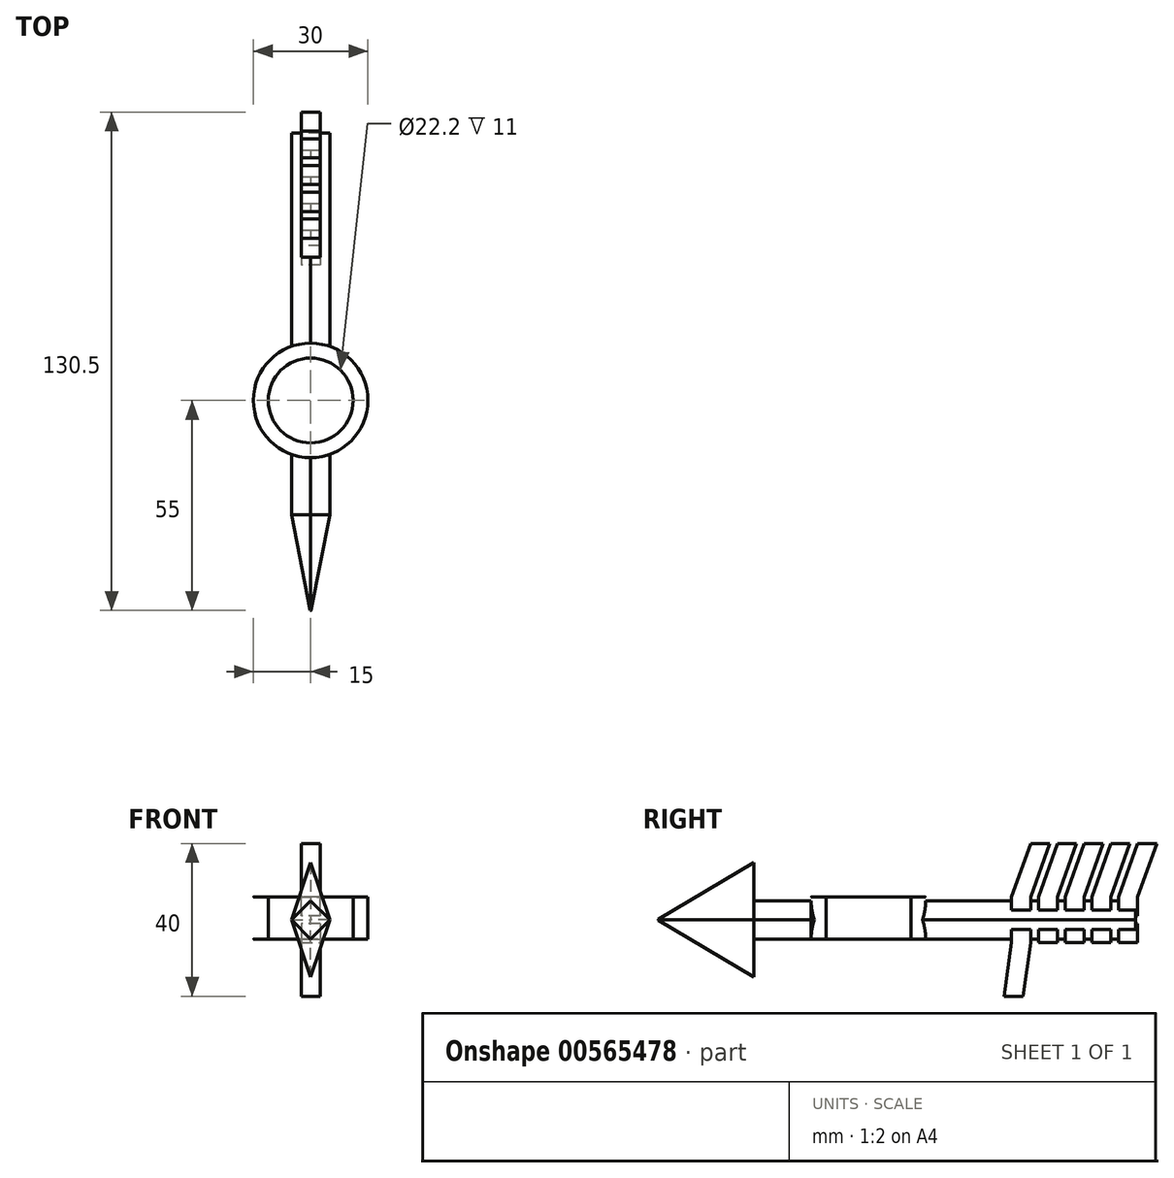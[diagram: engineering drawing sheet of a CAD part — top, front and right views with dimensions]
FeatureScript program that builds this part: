
annotation { "Feature Type Name" : "Feature", "Feature Type Description" : "" }
export const myFeature = defineFeature(function(context is Context, id is Id, definition is map)
    precondition{}
    {
        {
            var Q0;
            Q0=qCreatedBy(makeId("Front.planeOp"),FACE);
            var sketch = newSketch(context, id + "F0", { "sketchPlane" : qUnion([Q0])});
            skPoint(sketch, "E0", {"position": v(0, 15) * mm});
            skPoint(sketch, "E1", {"position": v(0, -15) * mm});
            skPoint(sketch, "E2", {"position": v(5, 0) * mm});
            skPoint(sketch, "E3", {"position": v(-5, 0) * mm});
            skLineSegment(sketch, "E4", {"start": v(0, 15) * mm, "end": v(-5, 0) * mm});
            skLineSegment(sketch, "E5", {"start": v(-5, 0) * mm, "end": v(0, -15) * mm});
            skLineSegment(sketch, "E6", {"start": v(0, -15) * mm, "end": v(5, 0) * mm});
            skLineSegment(sketch, "E7", {"start": v(5, 0) * mm, "end": v(0, 15) * mm});
            skSolve(sketch);
        }
        {
            var Q0;
            Q0=qCreatedBy(makeId("Front.planeOp"),FACE);
            cPlane(context, id + "F1", {"entities" : qUnion([Q0]), "cplaneType" : CPlaneType.OFFSET, "offset" : 25 * mm, "width" : 150 * mm, "height" : 150 * mm});
        }
        {
            var Q0;
            Q0=qCreatedBy(id+"F1.planeOp",FACE);
            var sketch = newSketch(context, id + "F2", { "sketchPlane" : qUnion([Q0])});
            skPoint(sketch, "E8", {"position": v(0, 0) * mm});
            skCircle(sketch, "E9", {"center": v(0, 0) * mm, "radius": 0.1 * mm});
            skPoint(sketch, "E10", {"position": v(0, 0.1) * mm});
            skPoint(sketch, "E11", {"position": v(0, -0.1) * mm});
            skPoint(sketch, "E12", {"position": v(-0.1, 0) * mm});
            skPoint(sketch, "E13", {"position": v(0.1, 0) * mm});
            skSolve(sketch);
        }
        {
            var Q0;
            Q0=makeQuery(id+"F0.imprint","IMPRINT",FACE,{"disambiguationData":[TD([[makeQuery(id+"F0.imprint","IMPRINT",EDGE,{"derivedFrom":sQuery(id+"F0.wireOp",EDGE,"E4")}),1.0]])]});
            var Q1;
            Q1=makeQuery(id+"F2.imprint","IMPRINT",FACE,{"disambiguationData":[TD([[makeQuery(id+"F2.imprint","IMPRINT",EDGE,{"derivedFrom":sQuery(id+"F2.wireOp",EDGE,"E9")}),1.0]])]});
            loft(context, id + "F3", {"sheetProfilesArray" : [{ "sheetProfileEntities" : qUnion([Q0]) }, { "sheetProfileEntities" : qUnion([Q1]) }]});
        }
        {
            var Q0;
            Q0=qCreatedBy(makeId("Front.planeOp"),FACE);
            var sketch = newSketch(context, id + "F4", { "sketchPlane" : qUnion([Q0])});
            skCircle(sketch, "E14.cCircle", {"center": v(0, 0) * mm, "radius": 5 * mm, "construction": true});
            skLineSegment(sketch, "E14.0", {"start": v(-5, 0) * mm, "end": v(0, 5) * mm});
            skLineSegment(sketch, "E14.1", {"start": v(0, 5) * mm, "end": v(5, 0) * mm});
            skLineSegment(sketch, "E14.2", {"start": v(5, 0) * mm, "end": v(0, -5) * mm});
            skLineSegment(sketch, "E14.3", {"start": v(0, -5) * mm, "end": v(-5, 0) * mm});
            skSolve(sketch);
        }
        {
            var Q0;
            Q0 = qSketchRegion(id + "F4", true);
            var Q1;
            Q1=makeQuery(id+"F4.imprint","IMPRINT",FACE,{"disambiguationData":[TD([[makeQuery(id+"F4.imprint","IMPRINT",EDGE,{"derivedFrom":sQuery(id+"F4.wireOp",EDGE,"E14.0")}),-1.0]])]});
            extrude(context, id + "F5", {"entities" : qUnion([Q0, Q1]), "operationType" : NewBodyOperationType.ADD, "oppositeDirection" : true, "depth" : 100 * mm, "offsetDistance" : 25 * mm});
        }
        {
            var Q0;
            Q0=qCreatedBy(makeId("Top.planeOp"),FACE);
            cPlane(context, id + "F6", {"entities" : qUnion([Q0]), "cplaneType" : CPlaneType.OFFSET, "offset" : 6 * mm, "width" : 150 * mm, "height" : 150 * mm});
        }
        {
            var Q0;
            Q0=qCreatedBy(id+"F6.planeOp",FACE);
            var sketch = newSketch(context, id + "F7", { "sketchPlane" : qUnion([Q0])});
            skPoint(sketch, "E15", {"position": v(0, 30) * mm});
            skCircle(sketch, "E16", {"center": v(0, 30) * mm, "radius": 15 * mm});
            skCircle(sketch, "E17", {"center": v(0, 30) * mm, "radius": 11 * mm});
            skSolve(sketch);
        }
        {
            var Q0;
            Q0 = qSketchRegion(id + "F7", true);
            extrude(context, id + "F8", {"entities" : qUnion([Q0]), "operationType" : NewBodyOperationType.ADD, "oppositeDirection" : true, "depth" : 11 * mm, "offsetDistance" : 25 * mm});
        }
        {
            var Q0;
            Q0=qCreatedBy(id+"F6.planeOp",FACE);
            var sketch = newSketch(context, id + "F9", { "sketchPlane" : qUnion([Q0])});
            skPoint(sketch, "E18", {"position": v(0, 30) * mm});
            skCircle(sketch, "E19", {"center": v(0, 30) * mm, "radius": 11.1 * mm});
            skSolve(sketch);
        }
        {
            var Q0;
            Q0=makeQuery(id+"F9.imprint","IMPRINT",FACE,{"disambiguationData":[TD([[makeQuery(id+"F9.imprint","IMPRINT",EDGE,{"derivedFrom":sQuery(id+"F9.wireOp",EDGE,"E19")}),1.0]])]});
            extrude(context, id + "F10", {"entities" : qUnion([Q0]), "operationType" : NewBodyOperationType.REMOVE, "endBound" : BoundingType.THROUGH_ALL, "oppositeDirection" : true, "depth" : 25 * mm, "offsetDistance" : 25 * mm});
        }
        {
            var Q0;
            Q0=qCreatedBy(id+"F6.planeOp",FACE);
            var sketch = newSketch(context, id + "F11", { "sketchPlane" : qUnion([Q0])});
            skPoint(sketch, "E20", {"position": v(0, 70) * mm});
            skLineSegment(sketch, "E21.bottom", {"start": v(2.5, 72.5) * mm, "end": v(-2.5, 72.5) * mm});
            skLineSegment(sketch, "E21.top", {"start": v(2.5, 67.5) * mm, "end": v(-2.5, 67.5) * mm});
            skLineSegment(sketch, "E21.left", {"start": v(2.5, 72.5) * mm, "end": v(2.5, 67.5) * mm});
            skLineSegment(sketch, "E21.right", {"start": v(-2.5, 72.5) * mm, "end": v(-2.5, 67.5) * mm});
            skPoint(sketch, "E22", {"position": v(-2.5, 67.5) * mm});
            skPoint(sketch, "E23", {"position": v(-2.5, 72.5) * mm});
            skPoint(sketch, "E24", {"position": v(2.5, 72.5) * mm});
            skPoint(sketch, "E25", {"position": v(2.5, 67.5) * mm});
            skPoint(sketch, "E26", {"position": v(0, 77) * mm});
            skPoint(sketch, "E27", {"position": v(0, 84) * mm});
            skPoint(sketch, "E28", {"position": v(0, 91) * mm});
            skPoint(sketch, "E29", {"position": v(0, 98) * mm});
            skLineSegment(sketch, "E30.bottom", {"start": v(2.5, 79.5) * mm, "end": v(-2.5, 79.5) * mm});
            skLineSegment(sketch, "E30.top", {"start": v(2.5, 74.5) * mm, "end": v(-2.5, 74.5) * mm});
            skLineSegment(sketch, "E30.left", {"start": v(2.5, 79.5) * mm, "end": v(2.5, 74.5) * mm});
            skLineSegment(sketch, "E30.right", {"start": v(-2.5, 79.5) * mm, "end": v(-2.5, 74.5) * mm});
            skLineSegment(sketch, "E31.bottom", {"start": v(2.5, 86.5) * mm, "end": v(-2.5, 86.5) * mm});
            skLineSegment(sketch, "E31.top", {"start": v(2.5, 81.5) * mm, "end": v(-2.5, 81.5) * mm});
            skLineSegment(sketch, "E31.left", {"start": v(2.5, 86.5) * mm, "end": v(2.5, 81.5) * mm});
            skLineSegment(sketch, "E31.right", {"start": v(-2.5, 86.5) * mm, "end": v(-2.5, 81.5) * mm});
            skLineSegment(sketch, "E32.bottom", {"start": v(2.5, 93.5) * mm, "end": v(-2.5, 93.5) * mm});
            skLineSegment(sketch, "E32.top", {"start": v(2.5, 88.5) * mm, "end": v(-2.5, 88.5) * mm});
            skLineSegment(sketch, "E32.left", {"start": v(2.5, 93.5) * mm, "end": v(2.5, 88.5) * mm});
            skLineSegment(sketch, "E32.right", {"start": v(-2.5, 93.5) * mm, "end": v(-2.5, 88.5) * mm});
            skLineSegment(sketch, "E33.bottom", {"start": v(2.5, 100.5) * mm, "end": v(-2.5, 100.5) * mm});
            skLineSegment(sketch, "E33.top", {"start": v(2.5, 95.5) * mm, "end": v(-2.5, 95.5) * mm});
            skLineSegment(sketch, "E33.left", {"start": v(2.5, 100.5) * mm, "end": v(2.5, 95.5) * mm});
            skLineSegment(sketch, "E33.right", {"start": v(-2.5, 100.5) * mm, "end": v(-2.5, 95.5) * mm});
            skPoint(sketch, "E34", {"position": v(-2.5, 74.5) * mm});
            skPoint(sketch, "E35", {"position": v(-2.5, 79.5) * mm});
            skPoint(sketch, "E36", {"position": v(2.5, 79.5) * mm});
            skPoint(sketch, "E37", {"position": v(2.5, 74.5) * mm});
            skPoint(sketch, "E38", {"position": v(-2.5, 81.5) * mm});
            skPoint(sketch, "E39", {"position": v(-2.5, 86.5) * mm});
            skPoint(sketch, "E40", {"position": v(2.5, 86.5) * mm});
            skPoint(sketch, "E41", {"position": v(2.5, 81.5) * mm});
            skPoint(sketch, "E42", {"position": v(-2.5, 88.5) * mm});
            skPoint(sketch, "E43", {"position": v(-2.5, 93.5) * mm});
            skPoint(sketch, "E44", {"position": v(2.5, 93.5) * mm});
            skPoint(sketch, "E45", {"position": v(2.5, 88.5) * mm});
            skPoint(sketch, "E46", {"position": v(-2.5, 95.5) * mm});
            skPoint(sketch, "E47", {"position": v(-2.5, 100.5) * mm});
            skPoint(sketch, "E48", {"position": v(2.5, 100.5) * mm});
            skPoint(sketch, "E49", {"position": v(2.5, 95.5) * mm});
            skSolve(sketch);
        }
        {
            var Q0;
            Q0=qCreatedBy(makeId("Top.planeOp"),FACE);
            cPlane(context, id + "F12", {"entities" : qUnion([Q0]), "cplaneType" : CPlaneType.OFFSET, "offset" : 20 * mm, "width" : 150 * mm, "height" : 150 * mm});
        }
        {
            var Q0;
            Q0=qCreatedBy(id+"F12.planeOp",FACE);
            var sketch = newSketch(context, id + "F13", { "sketchPlane" : qUnion([Q0])});
            skPoint(sketch, "E50", {"position": v(0, 75) * mm});
            skPoint(sketch, "E51", {"position": v(0, 82) * mm});
            skPoint(sketch, "E52", {"position": v(0, 89) * mm});
            skPoint(sketch, "E53", {"position": v(0, 96) * mm});
            skLineSegment(sketch, "E54", {"start": v(0, 0) * mm, "end": v(0, 100) * mm, "construction": true});
            skPoint(sketch, "E55", {"position": v(0, 103) * mm});
            skLineSegment(sketch, "E56.bottom", {"start": v(2.5, 77.5) * mm, "end": v(-2.5, 77.5) * mm});
            skLineSegment(sketch, "E56.top", {"start": v(2.5, 72.5) * mm, "end": v(-2.5, 72.5) * mm});
            skLineSegment(sketch, "E56.left", {"start": v(2.5, 77.5) * mm, "end": v(2.5, 72.5) * mm});
            skLineSegment(sketch, "E56.right", {"start": v(-2.5, 77.5) * mm, "end": v(-2.5, 72.5) * mm});
            skLineSegment(sketch, "E57.bottom", {"start": v(2.5, 84.5) * mm, "end": v(-2.5, 84.5) * mm});
            skLineSegment(sketch, "E57.top", {"start": v(2.5, 79.5) * mm, "end": v(-2.5, 79.5) * mm});
            skLineSegment(sketch, "E57.left", {"start": v(2.5, 84.5) * mm, "end": v(2.5, 79.5) * mm});
            skLineSegment(sketch, "E57.right", {"start": v(-2.5, 84.5) * mm, "end": v(-2.5, 79.5) * mm});
            skLineSegment(sketch, "E58.bottom", {"start": v(2.5, 91.5) * mm, "end": v(-2.5, 91.5) * mm});
            skLineSegment(sketch, "E58.top", {"start": v(2.5, 86.5) * mm, "end": v(-2.5, 86.5) * mm});
            skLineSegment(sketch, "E58.left", {"start": v(2.5, 91.5) * mm, "end": v(2.5, 86.5) * mm});
            skLineSegment(sketch, "E58.right", {"start": v(-2.5, 91.5) * mm, "end": v(-2.5, 86.5) * mm});
            skLineSegment(sketch, "E59.bottom", {"start": v(2.5, 98.5) * mm, "end": v(-2.5, 98.5) * mm});
            skLineSegment(sketch, "E59.top", {"start": v(2.5, 93.5) * mm, "end": v(-2.5, 93.5) * mm});
            skLineSegment(sketch, "E59.left", {"start": v(2.5, 98.5) * mm, "end": v(2.5, 93.5) * mm});
            skLineSegment(sketch, "E59.right", {"start": v(-2.5, 98.5) * mm, "end": v(-2.5, 93.5) * mm});
            skLineSegment(sketch, "E60.bottom", {"start": v(2.5, 105.5) * mm, "end": v(-2.5, 105.5) * mm});
            skLineSegment(sketch, "E60.top", {"start": v(2.5, 100.5) * mm, "end": v(-2.5, 100.5) * mm});
            skLineSegment(sketch, "E60.left", {"start": v(2.5, 105.5) * mm, "end": v(2.5, 100.5) * mm});
            skLineSegment(sketch, "E60.right", {"start": v(-2.5, 105.5) * mm, "end": v(-2.5, 100.5) * mm});
            skSolve(sketch);
        }
        {
            var Q0;
            Q0=makeQuery(id+"F11.imprint","IMPRINT",FACE,{"disambiguationData":[TD([[makeQuery(id+"F11.imprint","IMPRINT",EDGE,{"derivedFrom":sQuery(id+"F11.wireOp",EDGE,"E21.bottom")}),1.0]])]});
            var Q1;
            Q1=makeQuery(id+"F11.imprint","IMPRINT",FACE,{"disambiguationData":[TD([[makeQuery(id+"F11.imprint","IMPRINT",EDGE,{"derivedFrom":sQuery(id+"F11.wireOp",EDGE,"E30.bottom")}),1.0]])]});
            var Q2;
            Q2=makeQuery(id+"F11.imprint","IMPRINT",FACE,{"disambiguationData":[TD([[makeQuery(id+"F11.imprint","IMPRINT",EDGE,{"derivedFrom":sQuery(id+"F11.wireOp",EDGE,"E31.bottom")}),1.0]])]});
            var Q3;
            Q3=makeQuery(id+"F11.imprint","IMPRINT",FACE,{"disambiguationData":[TD([[makeQuery(id+"F11.imprint","IMPRINT",EDGE,{"derivedFrom":sQuery(id+"F11.wireOp",EDGE,"E32.bottom")}),1.0]])]});
            var Q4;
            Q4=makeQuery(id+"F11.imprint","IMPRINT",FACE,{"disambiguationData":[TD([[makeQuery(id+"F11.imprint","IMPRINT",EDGE,{"derivedFrom":sQuery(id+"F11.wireOp",EDGE,"E33.bottom")}),1.0]])]});
            extrude(context, id + "F14", {"entities" : qUnion([Q0, Q1, Q2, Q3, Q4]), "operationType" : NewBodyOperationType.ADD, "oppositeDirection" : true, "depth" : 5 * mm, "offsetDistance" : 25 * mm});
        }
        {
            var Q1;
            Q1=makeQuery(id+"F14.opExtrude","CAP_FACE",FACE,{"disambiguationData":[OSD([sQuery(id+"F11.wireOp",EDGE,"E21.bottom"),sQuery(id+"F11.wireOp",EDGE,"E21.top"),sQuery(id+"F11.wireOp",EDGE,"E21.left"),sQuery(id+"F11.wireOp",EDGE,"E21.right")])],"isStart":true});
            var Q2;
            Q2=makeQuery(id+"F13.imprint","IMPRINT",FACE,{"disambiguationData":[TD([[makeQuery(id+"F13.imprint","IMPRINT",EDGE,{"derivedFrom":sQuery(id+"F13.wireOp",EDGE,"E56.bottom")}),1.0]])]});
            loft(context, id + "F15", {"operationType" : NewBodyOperationType.ADD, "sheetProfilesArray" : [{ "sheetProfileEntities" : qUnion([Q1]) }, { "sheetProfileEntities" : qUnion([Q2]) }]});
        }
        {
            var Q1;
            Q1=makeQuery(id+"F14.opExtrude","CAP_FACE",FACE,{"disambiguationData":[OSD([sQuery(id+"F11.wireOp",EDGE,"E30.bottom"),sQuery(id+"F11.wireOp",EDGE,"E30.top"),sQuery(id+"F11.wireOp",EDGE,"E30.left"),sQuery(id+"F11.wireOp",EDGE,"E30.right")])],"isStart":true});
            var Q2;
            Q2=makeQuery(id+"F13.imprint","IMPRINT",FACE,{"disambiguationData":[TD([[makeQuery(id+"F13.imprint","IMPRINT",EDGE,{"derivedFrom":sQuery(id+"F13.wireOp",EDGE,"E57.bottom")}),1.0]])]});
            loft(context, id + "F16", {"operationType" : NewBodyOperationType.ADD, "sheetProfilesArray" : [{ "sheetProfileEntities" : qUnion([Q1]) }, { "sheetProfileEntities" : qUnion([Q2]) }]});
        }
        {
            var Q1;
            Q1=makeQuery(id+"F14.opExtrude","CAP_FACE",FACE,{"disambiguationData":[OSD([sQuery(id+"F11.wireOp",EDGE,"E31.bottom"),sQuery(id+"F11.wireOp",EDGE,"E31.top"),sQuery(id+"F11.wireOp",EDGE,"E31.left"),sQuery(id+"F11.wireOp",EDGE,"E31.right")])],"isStart":true});
            var Q2;
            Q2=makeQuery(id+"F13.imprint","IMPRINT",FACE,{"disambiguationData":[TD([[makeQuery(id+"F13.imprint","IMPRINT",EDGE,{"derivedFrom":sQuery(id+"F13.wireOp",EDGE,"E58.bottom")}),1.0]])]});
            loft(context, id + "F17", {"operationType" : NewBodyOperationType.ADD, "sheetProfilesArray" : [{ "sheetProfileEntities" : qUnion([Q1]) }, { "sheetProfileEntities" : qUnion([Q2]) }]});
        }
        {
            var Q1;
            Q1=makeQuery(id+"F14.opExtrude","CAP_FACE",FACE,{"disambiguationData":[OSD([sQuery(id+"F11.wireOp",EDGE,"E32.bottom"),sQuery(id+"F11.wireOp",EDGE,"E32.top"),sQuery(id+"F11.wireOp",EDGE,"E32.left"),sQuery(id+"F11.wireOp",EDGE,"E32.right")])],"isStart":true});
            var Q2;
            Q2=makeQuery(id+"F13.imprint","IMPRINT",FACE,{"disambiguationData":[TD([[makeQuery(id+"F13.imprint","IMPRINT",EDGE,{"derivedFrom":sQuery(id+"F13.wireOp",EDGE,"E59.bottom")}),1.0]])]});
            loft(context, id + "F18", {"operationType" : NewBodyOperationType.ADD, "sheetProfilesArray" : [{ "sheetProfileEntities" : qUnion([Q1]) }, { "sheetProfileEntities" : qUnion([Q2]) }]});
        }
        {
            var Q1;
            Q1=makeQuery(id+"F14.opExtrude","CAP_FACE",FACE,{"disambiguationData":[OSD([sQuery(id+"F11.wireOp",EDGE,"E33.bottom"),sQuery(id+"F11.wireOp",EDGE,"E33.top"),sQuery(id+"F11.wireOp",EDGE,"E33.left"),sQuery(id+"F11.wireOp",EDGE,"E33.right")])],"isStart":true});
            var Q2;
            Q2=makeQuery(id+"F13.imprint","IMPRINT",FACE,{"disambiguationData":[TD([[makeQuery(id+"F13.imprint","IMPRINT",EDGE,{"derivedFrom":sQuery(id+"F13.wireOp",EDGE,"E60.bottom")}),1.0]])]});
            loft(context, id + "F19", {"operationType" : NewBodyOperationType.ADD, "sheetProfilesArray" : [{ "sheetProfileEntities" : qUnion([Q1]) }, { "sheetProfileEntities" : qUnion([Q2]) }]});
        }
        {
            var Q0;
            Q0=qCreatedBy(makeId("Top.planeOp"),FACE);
            cPlane(context, id + "F20", {"entities" : qUnion([Q0]), "cplaneType" : CPlaneType.OFFSET, "offset" : 6 * mm, "oppositeDirection" : true, "width" : 150 * mm, "height" : 150 * mm});
        }
        {
            var Q0;
            Q0=qCreatedBy(id+"F20.planeOp",FACE);
            var sketch = newSketch(context, id + "F21", { "sketchPlane" : qUnion([Q0])});
            skPoint(sketch, "E61", {"position": v(0, 70) * mm});
            skPoint(sketch, "E62", {"position": v(0, 77) * mm});
            skPoint(sketch, "E63", {"position": v(0, 84) * mm});
            skPoint(sketch, "E64", {"position": v(0, 91) * mm});
            skPoint(sketch, "E65", {"position": v(0, 98) * mm});
            skLineSegment(sketch, "E66.bottom", {"start": v(-2.5, 67.5) * mm, "end": v(2.5, 67.5) * mm});
            skLineSegment(sketch, "E66.top", {"start": v(-2.5, 72.5) * mm, "end": v(2.5, 72.5) * mm});
            skLineSegment(sketch, "E66.left", {"start": v(-2.5, 67.5) * mm, "end": v(-2.5, 72.5) * mm});
            skLineSegment(sketch, "E66.right", {"start": v(2.5, 67.5) * mm, "end": v(2.5, 72.5) * mm});
            skLineSegment(sketch, "E67.bottom", {"start": v(-2.5, 74.5) * mm, "end": v(2.5, 74.5) * mm});
            skLineSegment(sketch, "E67.top", {"start": v(-2.5, 79.5) * mm, "end": v(2.5, 79.5) * mm});
            skLineSegment(sketch, "E67.left", {"start": v(-2.5, 74.5) * mm, "end": v(-2.5, 79.5) * mm});
            skLineSegment(sketch, "E67.right", {"start": v(2.5, 74.5) * mm, "end": v(2.5, 79.5) * mm});
            skLineSegment(sketch, "E68.bottom", {"start": v(-2.5, 81.5) * mm, "end": v(2.5, 81.5) * mm});
            skLineSegment(sketch, "E68.top", {"start": v(-2.5, 86.5) * mm, "end": v(2.5, 86.5) * mm});
            skLineSegment(sketch, "E68.left", {"start": v(-2.5, 81.5) * mm, "end": v(-2.5, 86.5) * mm});
            skLineSegment(sketch, "E68.right", {"start": v(2.5, 81.5) * mm, "end": v(2.5, 86.5) * mm});
            skLineSegment(sketch, "E69.bottom", {"start": v(-2.5, 88.5) * mm, "end": v(2.5, 88.5) * mm});
            skLineSegment(sketch, "E69.top", {"start": v(-2.5, 93.5) * mm, "end": v(2.5, 93.5) * mm});
            skLineSegment(sketch, "E69.left", {"start": v(-2.5, 88.5) * mm, "end": v(-2.5, 93.5) * mm});
            skLineSegment(sketch, "E69.right", {"start": v(2.5, 88.5) * mm, "end": v(2.5, 93.5) * mm});
            skLineSegment(sketch, "E70.bottom", {"start": v(-2.5, 95.5) * mm, "end": v(2.5, 95.5) * mm});
            skLineSegment(sketch, "E70.top", {"start": v(-2.5, 100.5) * mm, "end": v(2.5, 100.5) * mm});
            skLineSegment(sketch, "E70.left", {"start": v(-2.5, 95.5) * mm, "end": v(-2.5, 100.5) * mm});
            skLineSegment(sketch, "E70.right", {"start": v(2.5, 95.5) * mm, "end": v(2.5, 100.5) * mm});
            skSolve(sketch);
        }
        {
            var Q0;
            Q0 = qSketchRegion(id + "F21", true);
            extrude(context, id + "F22", {"entities" : qUnion([Q0]), "operationType" : NewBodyOperationType.ADD, "depth" : 5 * mm, "offsetDistance" : 25 * mm});
        }
        {
            var Q0;
            Q0=qCreatedBy(makeId("Top.planeOp"),FACE);
            cPlane(context, id + "F23", {"entities" : qUnion([Q0]), "cplaneType" : CPlaneType.OFFSET, "offset" : 20 * mm, "oppositeDirection" : true, "width" : 150 * mm, "height" : 150 * mm});
        }
        {
            var Q0;
            Q0=qCreatedBy(id+"F23.planeOp",FACE);
            var sketch = newSketch(context, id + "F24", { "sketchPlane" : qUnion([Q0])});
            skPoint(sketch, "E71", {"position": v(0, 68) * mm});
            skPoint(sketch, "E72", {"position": v(0, 75) * mm});
            skPoint(sketch, "E73", {"position": v(0, 83.73) * mm});
            skPoint(sketch, "E74", {"position": v(0, 90.86) * mm});
            skPoint(sketch, "E75", {"position": v(0, 98.09) * mm});
            skLineSegment(sketch, "E76.bottom", {"start": v(2.5, 77.5) * mm, "end": v(-2.5, 77.5) * mm});
            skLineSegment(sketch, "E76.top", {"start": v(2.5, 72.5) * mm, "end": v(-2.5, 72.5) * mm});
            skLineSegment(sketch, "E76.left", {"start": v(2.5, 77.5) * mm, "end": v(2.5, 72.5) * mm});
            skLineSegment(sketch, "E76.right", {"start": v(-2.5, 77.5) * mm, "end": v(-2.5, 72.5) * mm});
            skLineSegment(sketch, "E77.bottom", {"start": v(2.5, 70.5) * mm, "end": v(-2.5, 70.5) * mm});
            skLineSegment(sketch, "E77.top", {"start": v(2.5, 65.5) * mm, "end": v(-2.5, 65.5) * mm});
            skLineSegment(sketch, "E77.left", {"start": v(2.5, 70.5) * mm, "end": v(2.5, 65.5) * mm});
            skLineSegment(sketch, "E77.right", {"start": v(-2.5, 70.5) * mm, "end": v(-2.5, 65.5) * mm});
            skSolve(sketch);
        }
        {
            var Q1;
            Q1=makeQuery(id+"F22.opExtrude","CAP_FACE",FACE,{"disambiguationData":[OSD([sQuery(id+"F21.wireOp",EDGE,"E66.bottom"),sQuery(id+"F21.wireOp",EDGE,"E66.top"),sQuery(id+"F21.wireOp",EDGE,"E66.left"),sQuery(id+"F21.wireOp",EDGE,"E66.right")])],"isStart":true});
            var Q2;
            Q2=makeQuery(id+"F24.imprint","IMPRINT",FACE,{"disambiguationData":[TD([[makeQuery(id+"F24.imprint","IMPRINT",EDGE,{"derivedFrom":sQuery(id+"F24.wireOp",EDGE,"E77.bottom")}),1.0]])]});
            loft(context, id + "F25", {"operationType" : NewBodyOperationType.ADD, "sheetProfilesArray" : [{ "sheetProfileEntities" : qUnion([Q1]) }, { "sheetProfileEntities" : qUnion([Q2]) }]});
        }
    });
